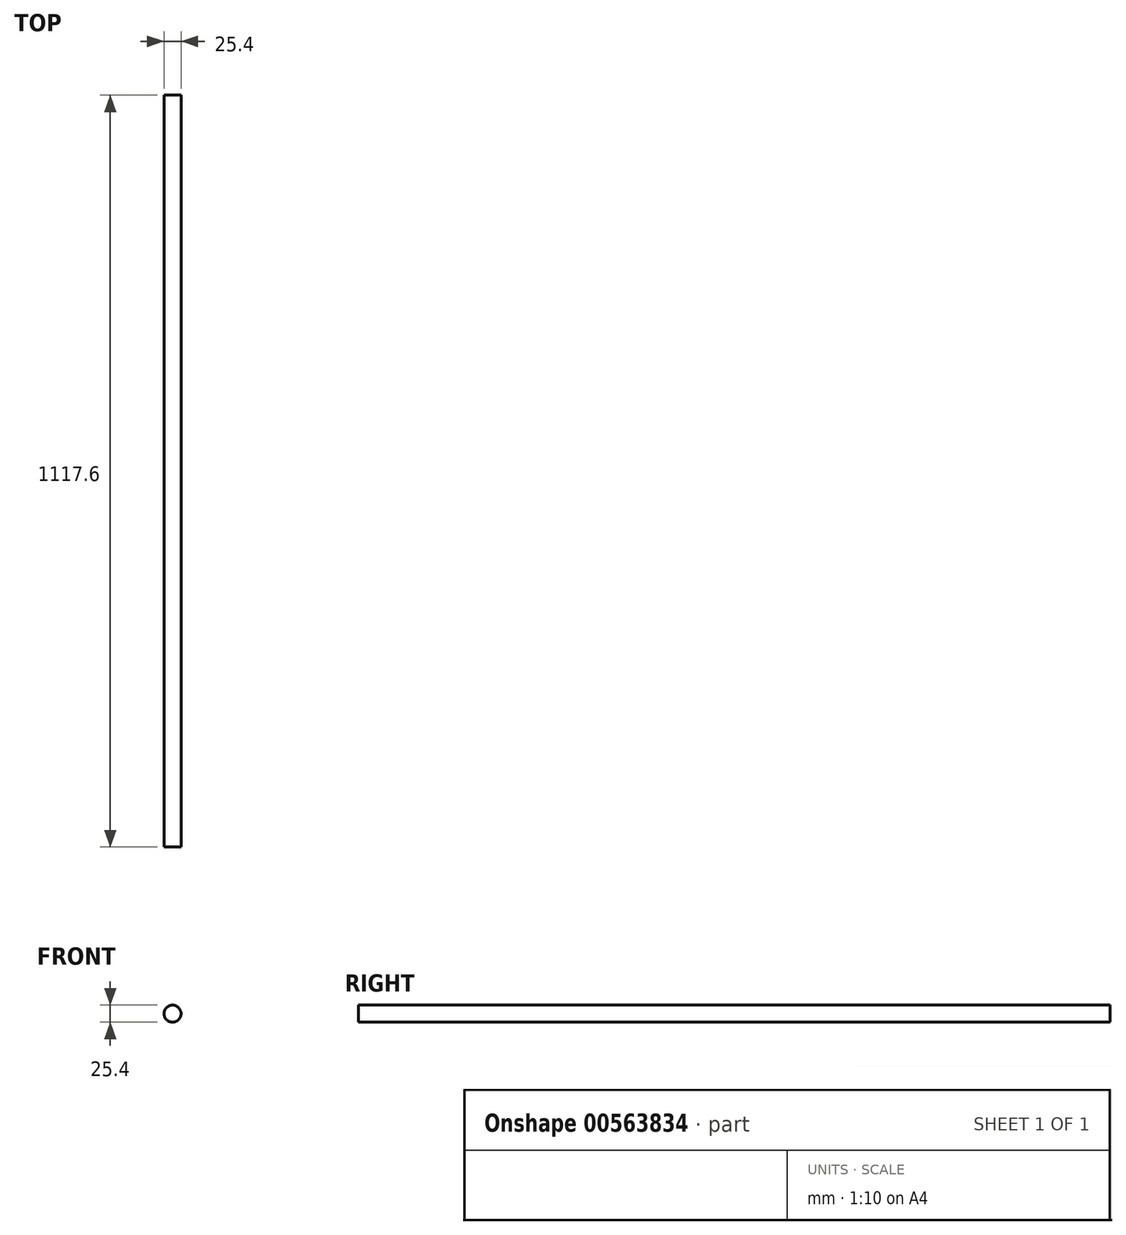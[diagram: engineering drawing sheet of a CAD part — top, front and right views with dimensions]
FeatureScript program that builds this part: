
annotation { "Feature Type Name" : "Feature", "Feature Type Description" : "" }
export const myFeature = defineFeature(function(context is Context, id is Id, definition is map)
    precondition{}
    {
        {
            var Q0;
            Q0=qCreatedBy(makeId("Front.planeOp"),FACE);
            var sketch = newSketch(context, id + "F0", { "sketchPlane" : qUnion([Q0])});
            skCircle(sketch, "E0", {"center": v(0, 0) * mm, "radius": 12.7 * mm});
            skSolve(sketch);
        }
        {
            var Q0;
            Q0=makeQuery(id+"F0.imprint","IMPRINT",FACE,{"disambiguationData":[TD([[makeQuery(id+"F0.imprint","IMPRINT",EDGE,{"derivedFrom":sQuery(id+"F0.wireOp",EDGE,"E0")}),1.0]])]});
            extrude(context, id + "F1", {"entities" : qUnion([Q0]), "endBound" : BoundingType.SYMMETRIC, "depth" : 1117.6 * mm, "offsetDistance" : 25.4 * mm});
        }
    });
